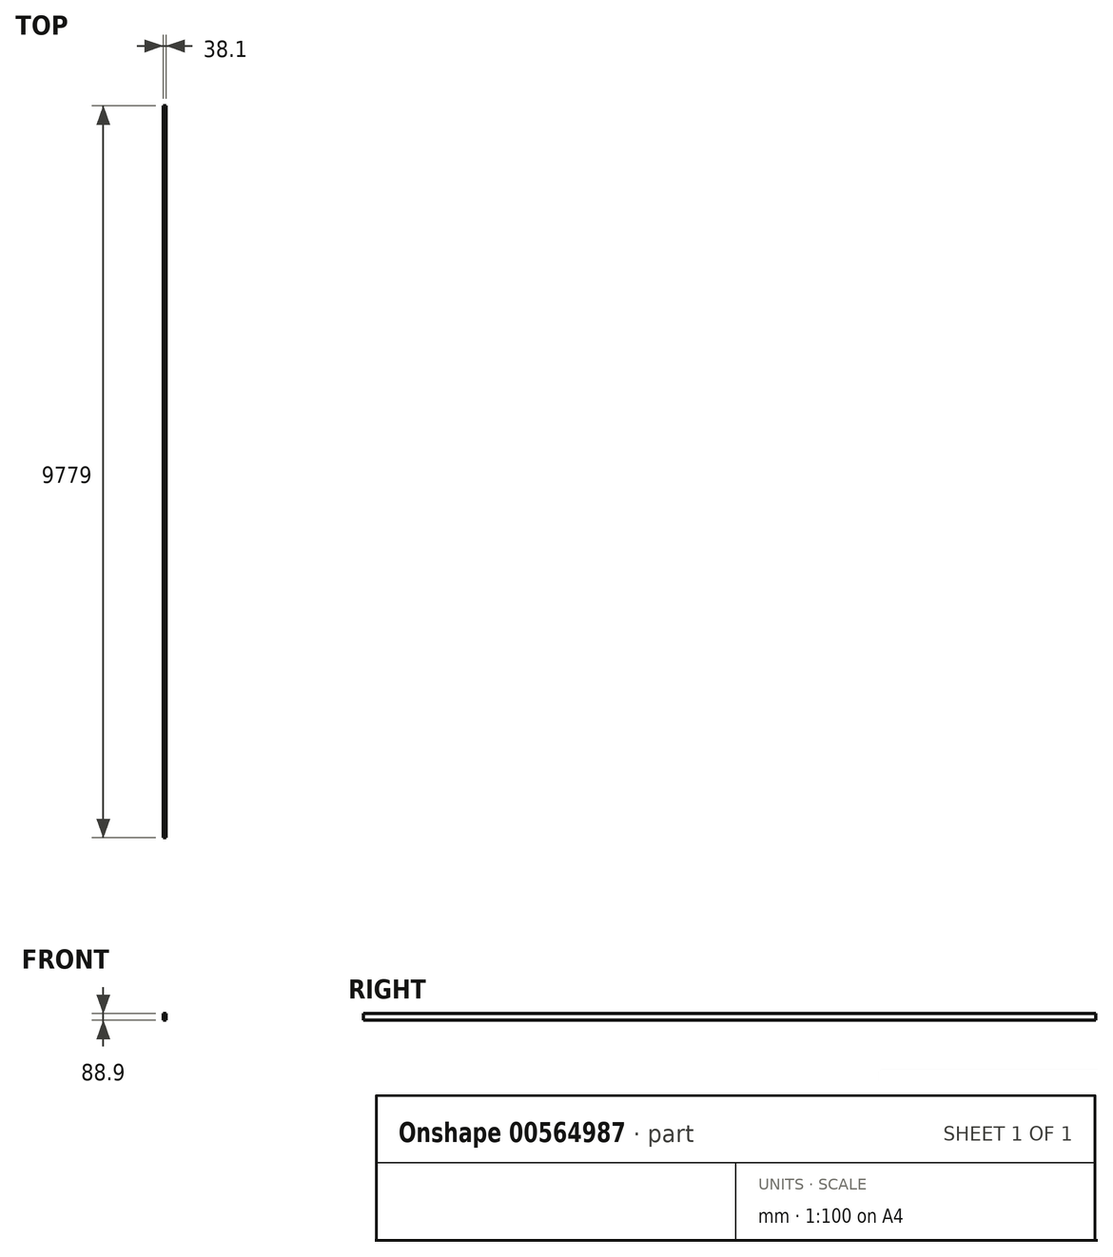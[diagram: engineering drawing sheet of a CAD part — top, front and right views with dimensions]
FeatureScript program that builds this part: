
annotation { "Feature Type Name" : "Feature", "Feature Type Description" : "" }
export const myFeature = defineFeature(function(context is Context, id is Id, definition is map)
    precondition{}
    {
        {
            var Q0;
            Q0=qCreatedBy(makeId("Front.planeOp"),FACE);
            var sketch = newSketch(context, id + "F0", { "sketchPlane" : qUnion([Q0])});
            skLineSegment(sketch, "E0.bottom", {"start": v(0, 0) * mm, "end": v(38.1, 0) * mm});
            skLineSegment(sketch, "E0.top", {"start": v(0, 88.9) * mm, "end": v(38.1, 88.9) * mm});
            skLineSegment(sketch, "E0.left", {"start": v(0, 0) * mm, "end": v(0, 88.9) * mm});
            skLineSegment(sketch, "E0.right", {"start": v(38.1, 0) * mm, "end": v(38.1, 88.9) * mm});
            skSolve(sketch);
        }
        {
            var Q0;
            Q0 = qSketchRegion(id + "F0", true);
            extrude(context, id + "F1", {"entities" : qUnion([Q0]), "depth" : 9779 * mm, "offsetDistance" : 25.4 * mm});
        }
    });
